# Revit family: Electronics_Visual-Projectors_ViewSonic_The-ViewSonicR-LS820-Projectors
name_source: partatom
category: Electrical Equipment
revit_build: Autodesk Revit 2015 (Build: 20140606_1530(x64)
units: mm (PartAtom-declared; Revit-internal decimal feet)

## types (1)
- LS820
    Assembly Code = D50
    BIMobject category = Visual - Projectors
    BIMobject category code = electronics-visual-projectors
    BIMobject main category = Electronics
    BIMobject main category code = electronics
    BOSUseNativeGeometries = 1
    Brand url = https://www.viewsonic.com
    Covering Color = Plastic - Viewsonic - Black
    Description = Delivering incredible color accuracy and stunning, razor-sharp images, the ViewSonic® LS820 laser projector is the ideal ultra-short throw projector for the high-end home theater. With a 0.23 ultra-short throw ratio, this projector can be placed on your home entertainment stand, just inches away from a wall or screen, and project an immersive 100” image. And with stunning 1080p resolution, and color accuracy, this projector delivers an amazing cinema-like experience. Utilizing the latest laser light technology, the LS820 is virtually maintenance-free, allowing you to enjoy long hours of movies or extensive gaming sessions. The LS820 also features a hidden PortAll® compartment which accommodates additional accessories such as a wireless streaming device, or PC stick. Powered by SuperColor™ technology for true-to-life images, and SonicExpert® technology for incredibly clear sound, the LS820 delivers an immersive audiovisual performance for any home theater.
    Design country = Taiwan
    Edition number = 1
    Keynote = V90
    Manufacturer = ViewSonic
    Manufacturer country = Taiwan
    Manufacturer name = ViewSonic
    Model = viewsonic_ls820
    Product Guid = 442d1c3a-75cc-4b36-bf00-2a03c177c07c
    Product SKU = viewsonic_ls820
    Product data url = https://bimobject.com
    Product family = Electronics
    Product group = Projectors
    Product name = The ViewSonic® LS820 Projector
    Product url = https://www.viewsonic.com
    Projection Angle = 25.00°
    QR code = http://bimobject.com
    URL = www.viewsonic.com
    a = Image Aspect Ratio : "4  - 3"
    b = Image Aspect Ratio : "16 - 9"
    c = Image Aspect Ratio : "16 - 10"

## geometry (parser evidence)
native form markers: Blend x2, Sweep x6
no freeform markers — native parametric forms only
